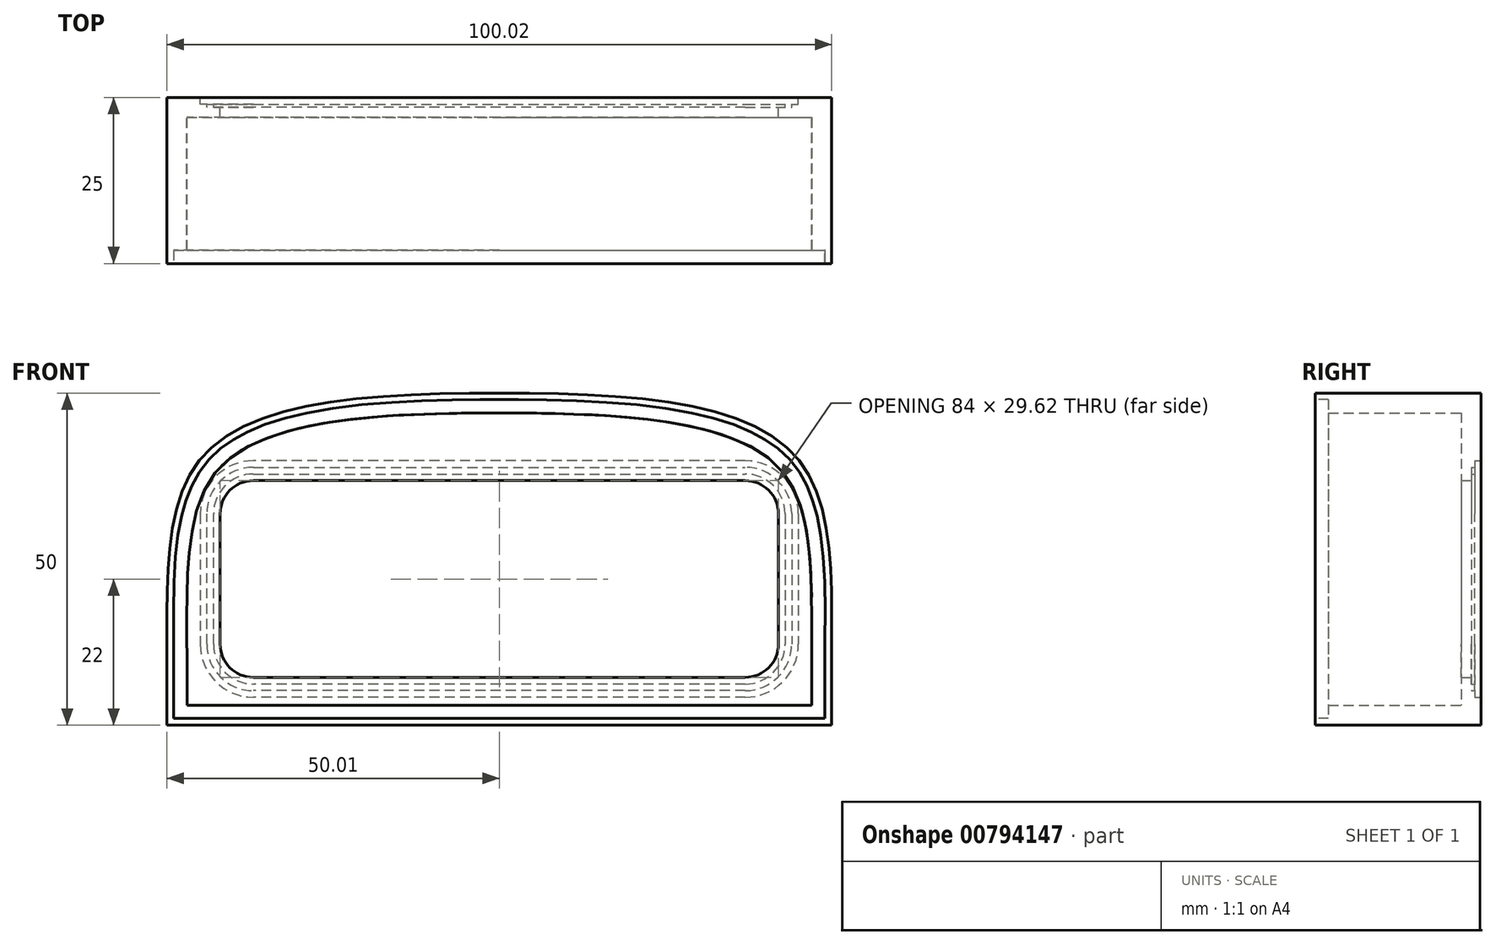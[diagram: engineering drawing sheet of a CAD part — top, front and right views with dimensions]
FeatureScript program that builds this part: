
annotation { "Feature Type Name" : "Feature", "Feature Type Description" : "" }
export const myFeature = defineFeature(function(context is Context, id is Id, definition is map)
    precondition{}
    {
        {
            var Q0;
            Q0=qCreatedBy(makeId("Front.planeOp"),FACE);
            var sketch = newSketch(context, id + "F0", { "sketchPlane" : qUnion([Q0])});
            skLineSegment(sketch, "E0.bottom", {"start": v(-50, 28) * mm, "end": v(50, 28) * mm, "construction": true});
            skLineSegment(sketch, "E0.top", {"start": v(-50, -22) * mm, "end": v(50, -22) * mm, "construction": true});
            skLineSegment(sketch, "E0.left", {"start": v(-50, 28) * mm, "end": v(-50, -22) * mm, "construction": true});
            skLineSegment(sketch, "E0.right", {"start": v(50, 28) * mm, "end": v(50, -22) * mm, "construction": true});
            skFitSpline(sketch, "E1", {"points": [v(0, 28) * mm, v(-44.35, 18.74) * mm, v(-50, -12) * mm], "startDerivative": vector(-104.26, 0) * mm, "endDerivative": vector(-0.26, -79.35) * mm});
            skFitSpline(sketch, "E2.MirrorCS", {"points": [v(0, 28) * mm, v(44.35, 18.74) * mm, v(50, -12) * mm], "startDerivative": vector(104.26, 0) * mm, "endDerivative": vector(0.26, -79.35) * mm});
            skFitSpline(sketch, "E3.MirrorCS", {"points": [v(0, 28) * mm, v(-44.35, 18.74) * mm, v(-50, -12) * mm], "startDerivative": vector(-104.26, 0) * mm, "endDerivative": vector(-0.26, -79.35) * mm});
            skFitSpline(sketch, "E4.MirrorCS", {"points": [v(0, 28) * mm, v(-44.35, 18.74) * mm, v(-50, -12) * mm], "startDerivative": vector(-104.26, 0) * mm, "endDerivative": vector(-0.26, -79.35) * mm});
            skLineSegment(sketch, "E5.bottom", {"start": v(37, 14.81) * mm, "end": v(-37, 14.81) * mm, "construction": true});
            skLineSegment(sketch, "E5.top", {"start": v(37, -14.81) * mm, "end": v(-37, -14.81) * mm, "construction": true});
            skLineSegment(sketch, "E5.left", {"start": v(42, 9.81) * mm, "end": v(42, -9.81) * mm, "construction": true});
            skLineSegment(sketch, "E5.right", {"start": v(-42, 9.81) * mm, "end": v(-42, -9.81) * mm, "construction": true});
            skPoint(sketch, "E5.middle", {"position": v(0, 0) * mm});
            skPoint(sketch, "E6.visualSharp", {"position": v(-41.6, 15.19) * mm});
            skArc(sketch, "E6.filletArc", {"start": v(-37, 14.81) * mm, "mid": v(-40.54, 13.35) * mm, "end": v(-42, 9.81) * mm, "construction": true});
            skPoint(sketch, "E7.visualSharp", {"position": v(-42, -14.81) * mm});
            skArc(sketch, "E7.filletArc", {"start": v(-42, -9.81) * mm, "mid": v(-40.54, -13.35) * mm, "end": v(-37, -14.81) * mm, "construction": true});
            skPoint(sketch, "E8.visualSharp", {"position": v(42, -14.81) * mm});
            skArc(sketch, "E8.filletArc", {"start": v(37, -14.81) * mm, "mid": v(40.54, -13.35) * mm, "end": v(42, -9.81) * mm, "construction": true});
            skPoint(sketch, "E9.visualSharp", {"position": v(42, 14.81) * mm});
            skArc(sketch, "E9.filletArc", {"start": v(42, 9.81) * mm, "mid": v(40.54, 13.35) * mm, "end": v(37, 14.81) * mm, "construction": true});
            skLineSegment(sketch, "E10", {"start": v(-50, -12) * mm, "end": v(-50, -22) * mm});
            skLineSegment(sketch, "E11", {"start": v(-50, -22) * mm, "end": v(50, -22) * mm});
            skLineSegment(sketch, "E12", {"start": v(50, -12) * mm, "end": v(50, -22) * mm});
            skSolve(sketch);
        }
        {
            var Q0;
            Q0=makeQuery(id+"F0.imprint","IMPRINT",FACE,{"disambiguationData":[TD([[makeQuery(id+"F0.imprint","IMPRINT",EDGE,{"derivedFrom":sQuery(id+"F0.wireOp",EDGE,"E2.MirrorCS")}),-1.0]])]});
            extrude(context, id + "F1", {"entities" : qUnion([Q0]), "depth" : 25 * mm, "offsetDistance" : 25 * mm});
        }
        {
            var Q0;
            Q0=makeQuery(id+"F1.opExtrude","CAP_FACE",FACE,{"disambiguationData":[OSD([sQuery(id+"F0.wireOp",EDGE,"E2.MirrorCS"),sQuery(id+"F0.wireOp",EDGE,"E4.MirrorCS"),sQuery(id+"F0.wireOp",EDGE,"E10"),sQuery(id+"F0.wireOp",EDGE,"E11"),sQuery(id+"F0.wireOp",EDGE,"E12")])],"isStart":false});
            shell(context, id + "F2", {"entities" : qUnion([Q0]), "thickness" : 3 * mm});
        }
        {
            var Q0;
            Q0=qCreatedBy(makeId("Front.planeOp"),FACE);
            var sketch = newSketch(context, id + "F3", { "sketchPlane" : qUnion([Q0])});
            skLineSegment(sketch, "E13.0", {"start": v(37, 14.81) * mm, "end": v(-37, 14.81) * mm});
            skArc(sketch, "E14.0", {"start": v(42, 9.81) * mm, "mid": v(40.54, 13.35) * mm, "end": v(37, 14.81) * mm});
            skLineSegment(sketch, "E14.1", {"start": v(42, 9.81) * mm, "end": v(42, -9.81) * mm});
            skArc(sketch, "E14.2", {"start": v(37, -14.81) * mm, "mid": v(40.54, -13.35) * mm, "end": v(42, -9.81) * mm});
            skLineSegment(sketch, "E14.3", {"start": v(37, -14.81) * mm, "end": v(-37, -14.81) * mm});
            skArc(sketch, "E14.4", {"start": v(-42, -9.81) * mm, "mid": v(-40.54, -13.35) * mm, "end": v(-37, -14.81) * mm});
            skLineSegment(sketch, "E14.5", {"start": v(-42, 9.81) * mm, "end": v(-42, -9.81) * mm});
            skArc(sketch, "E14.6", {"start": v(-37, 14.81) * mm, "mid": v(-40.54, 13.35) * mm, "end": v(-42, 9.81) * mm});
            skSolve(sketch);
        }
        {
            var Q0;
            Q0=makeQuery(id+"F3.imprint","IMPRINT",FACE,{"disambiguationData":[TD([[makeQuery(id+"F3.imprint","IMPRINT",EDGE,{"derivedFrom":sQuery(id+"F3.wireOp",EDGE,"E13.0")}),1.0]])]});
            extrude(context, id + "F4", {"entities" : qUnion([Q0]), "operationType" : NewBodyOperationType.REMOVE, "endBound" : BoundingType.UP_TO_NEXT, "depth" : 25 * mm, "offsetDistance" : 25 * mm});
        }
        {
            var Q0;
            Q0=makeQuery(id+"F1.opExtrude","CAP_FACE",FACE,{"disambiguationData":[OSD([sQuery(id+"F0.wireOp",EDGE,"E2.MirrorCS"),sQuery(id+"F0.wireOp",EDGE,"E4.MirrorCS"),sQuery(id+"F0.wireOp",EDGE,"E10"),sQuery(id+"F0.wireOp",EDGE,"E11"),sQuery(id+"F0.wireOp",EDGE,"E12")])],"isStart":true});
            var sketch = newSketch(context, id + "F5", { "sketchPlane" : qUnion([Q0])});
            skArc(sketch, "E15.0", {"start": v(-45, 9.81) * mm, "mid": v(-42.66, 15.47) * mm, "end": v(-37, 17.81) * mm});
            skLineSegment(sketch, "E15.1", {"start": v(-45, 9.81) * mm, "end": v(-45, -9.81) * mm});
            skLineSegment(sketch, "E15.2", {"start": v(-37, 17.81) * mm, "end": v(37, 17.81) * mm});
            skArc(sketch, "E15.3", {"start": v(-37, -17.81) * mm, "mid": v(-42.66, -15.47) * mm, "end": v(-45, -9.81) * mm});
            skArc(sketch, "E15.4", {"start": v(37, 17.81) * mm, "mid": v(42.66, 15.47) * mm, "end": v(45, 9.81) * mm});
            skLineSegment(sketch, "E15.5", {"start": v(45, 9.81) * mm, "end": v(45, -9.81) * mm});
            skArc(sketch, "E15.6", {"start": v(45, -9.81) * mm, "mid": v(42.66, -15.47) * mm, "end": v(37, -17.81) * mm});
            skLineSegment(sketch, "E15.7", {"start": v(-37, -17.81) * mm, "end": v(37, -17.81) * mm});
            skSolve(sketch);
        }
        {
            var Q0;
            Q0 = qSketchRegion(id + "F5", true);
            extrude(context, id + "F6", {"entities" : qUnion([Q0]), "operationType" : NewBodyOperationType.REMOVE, "oppositeDirection" : true, "depth" : 1 * mm, "offsetDistance" : 25 * mm});
        }
        {
            var Q0;
            Q0=makeQuery(id+"F6.boolean.opBoolean","COPY",FACE,{"derivedFrom":makeQuery(id+"F6.opExtrude","CAP_FACE",FACE,{"disambiguationData":[OSD([sQuery(id+"F5.wireOp",EDGE,"E15.0"),sQuery(id+"F5.wireOp",EDGE,"E15.1"),sQuery(id+"F5.wireOp",EDGE,"E15.2"),sQuery(id+"F5.wireOp",EDGE,"E15.3"),sQuery(id+"F5.wireOp",EDGE,"E15.4"),sQuery(id+"F5.wireOp",EDGE,"E15.5"),sQuery(id+"F5.wireOp",EDGE,"E15.6"),sQuery(id+"F5.wireOp",EDGE,"E15.7")])],"isStart":false})});
            var sketch = newSketch(context, id + "F7", { "sketchPlane" : qUnion([Q0])});
            skLineSegment(sketch, "E16.0", {"start": v(-44, 9.81) * mm, "end": v(-44, -9.81) * mm});
            skArc(sketch, "E16.1", {"start": v(-37, 16.81) * mm, "mid": v(-41.95, 14.76) * mm, "end": v(-44, 9.81) * mm});
            skArc(sketch, "E16.2", {"start": v(-44, -9.81) * mm, "mid": v(-41.95, -14.76) * mm, "end": v(-37, -16.81) * mm});
            skLineSegment(sketch, "E16.3", {"start": v(37, 16.81) * mm, "end": v(-37, 16.81) * mm});
            skLineSegment(sketch, "E16.4", {"start": v(-37, -16.81) * mm, "end": v(37, -16.81) * mm});
            skArc(sketch, "E16.5", {"start": v(37, -16.81) * mm, "mid": v(41.95, -14.76) * mm, "end": v(44, -9.81) * mm});
            skLineSegment(sketch, "E16.6", {"start": v(44, -9.81) * mm, "end": v(44, 9.81) * mm});
            skArc(sketch, "E16.7", {"start": v(44, 9.81) * mm, "mid": v(41.95, 14.76) * mm, "end": v(37, 16.81) * mm});
            skLineSegment(sketch, "E17.0", {"start": v(-43, 9.81) * mm, "end": v(-43, -9.81) * mm});
            skArc(sketch, "E17.1", {"start": v(-37, 15.81) * mm, "mid": v(-41.24, 14.05) * mm, "end": v(-43, 9.81) * mm});
            skArc(sketch, "E17.2", {"start": v(-43, -9.81) * mm, "mid": v(-41.24, -14.05) * mm, "end": v(-37, -15.81) * mm});
            skLineSegment(sketch, "E17.3", {"start": v(37, 15.81) * mm, "end": v(-37, 15.81) * mm});
            skLineSegment(sketch, "E17.4", {"start": v(-37, -15.81) * mm, "end": v(37, -15.81) * mm});
            skArc(sketch, "E17.5", {"start": v(37, -15.81) * mm, "mid": v(41.24, -14.05) * mm, "end": v(43, -9.81) * mm});
            skLineSegment(sketch, "E17.6", {"start": v(43, -9.81) * mm, "end": v(43, 9.81) * mm});
            skArc(sketch, "E17.7", {"start": v(43, 9.81) * mm, "mid": v(41.24, 14.05) * mm, "end": v(37, 15.81) * mm});
            skSolve(sketch);
        }
        {
            var Q0;
            Q0=makeQuery(id+"F7.imprint","IMPRINT",FACE,{"disambiguationData":[TD([[makeQuery(id+"F7.imprint","IMPRINT",EDGE,{"derivedFrom":sQuery(id+"F7.wireOp",EDGE,"E16.0")}),1.0]])]});
            extrude(context, id + "F8", {"entities" : qUnion([Q0]), "operationType" : NewBodyOperationType.REMOVE, "oppositeDirection" : true, "depth" : .5 * mm, "offsetDistance" : 25 * mm});
        }
        {
            var Q0;
            Q0=makeQuery(id+"F1.opExtrude","CAP_FACE",FACE,{"disambiguationData":[OSD([sQuery(id+"F0.wireOp",EDGE,"E2.MirrorCS"),sQuery(id+"F0.wireOp",EDGE,"E4.MirrorCS"),sQuery(id+"F0.wireOp",EDGE,"E10"),sQuery(id+"F0.wireOp",EDGE,"E11"),sQuery(id+"F0.wireOp",EDGE,"E12")])],"isStart":false});
            var sketch = newSketch(context, id + "F9", { "sketchPlane" : qUnion([Q0])});
            skLineSegment(sketch, "E18.0", {"start": v(-49, -12) * mm, "end": v(-49, -21) * mm});
            skFitSpline(sketch, "E18.1", {"points": [v(0, 27) * mm, v(-1.54, 27) * mm, v(-4.62, 26.99) * mm, v(-9.26, 26.9) * mm, v(-13.9, 26.73) * mm, v(-18.55, 26.44) * mm, v(-23.23, 25.96) * mm, v(-27.11, 25.37) * mm, v(-30.21, 24.73) * mm, v(-32.54, 24.13) * mm, v(-34.86, 23.4) * mm, v(-36.77, 22.66) * mm, v(-38.27, 21.95) * mm, v(-39.38, 21.36) * mm, v(-40.48, 20.7) * mm, v(-41.53, 19.96) * mm, v(-42.54, 19.14) * mm, v(-43.5, 18.21) * mm, v(-44.39, 17.18) * mm, v(-45.15, 16.1) * mm, v(-45.82, 14.98) * mm, v(-46.39, 13.81) * mm, v(-46.88, 12.62) * mm, v(-47.29, 11.43) * mm, v(-47.63, 10.23) * mm, v(-48, 8.64) * mm, v(-48.36, 6.65) * mm, v(-48.65, 4.27) * mm, v(-48.9, 1.11) * mm, v(-49, -2.79) * mm, v(-49, -7.42) * mm, v(-49, -10.48) * mm, v(-49, -12) * mm]});
            skLineSegment(sketch, "E18.2", {"start": v(-49, -21) * mm, "end": v(49, -21) * mm});
            skLineSegment(sketch, "E18.3", {"start": v(49, -12) * mm, "end": v(49, -21) * mm});
            skFitSpline(sketch, "E18.4", {"points": [v(0, 27) * mm, v(1.54, 27) * mm, v(4.62, 26.99) * mm, v(9.26, 26.9) * mm, v(13.9, 26.73) * mm, v(18.55, 26.44) * mm, v(23.23, 25.96) * mm, v(27.11, 25.37) * mm, v(30.21, 24.73) * mm, v(32.54, 24.13) * mm, v(34.86, 23.4) * mm, v(36.77, 22.66) * mm, v(38.27, 21.95) * mm, v(39.38, 21.36) * mm, v(40.48, 20.7) * mm, v(41.53, 19.96) * mm, v(42.54, 19.14) * mm, v(43.5, 18.21) * mm, v(44.39, 17.18) * mm, v(45.15, 16.1) * mm, v(45.82, 14.98) * mm, v(46.39, 13.81) * mm, v(46.88, 12.62) * mm, v(47.29, 11.43) * mm, v(47.63, 10.23) * mm, v(48, 8.64) * mm, v(48.36, 6.65) * mm, v(48.65, 4.27) * mm, v(48.9, 1.11) * mm, v(49, -2.79) * mm, v(49, -7.42) * mm, v(49, -10.48) * mm, v(49, -12) * mm]});
            skSolve(sketch);
        }
        {
            var Q0;
            Q0 = qSketchRegion(id + "F9", true);
            extrude(context, id + "F10", {"entities" : qUnion([Q0]), "operationType" : NewBodyOperationType.REMOVE, "oppositeDirection" : true, "depth" : 2 * mm, "offsetDistance" : 25 * mm});
        }
    });
